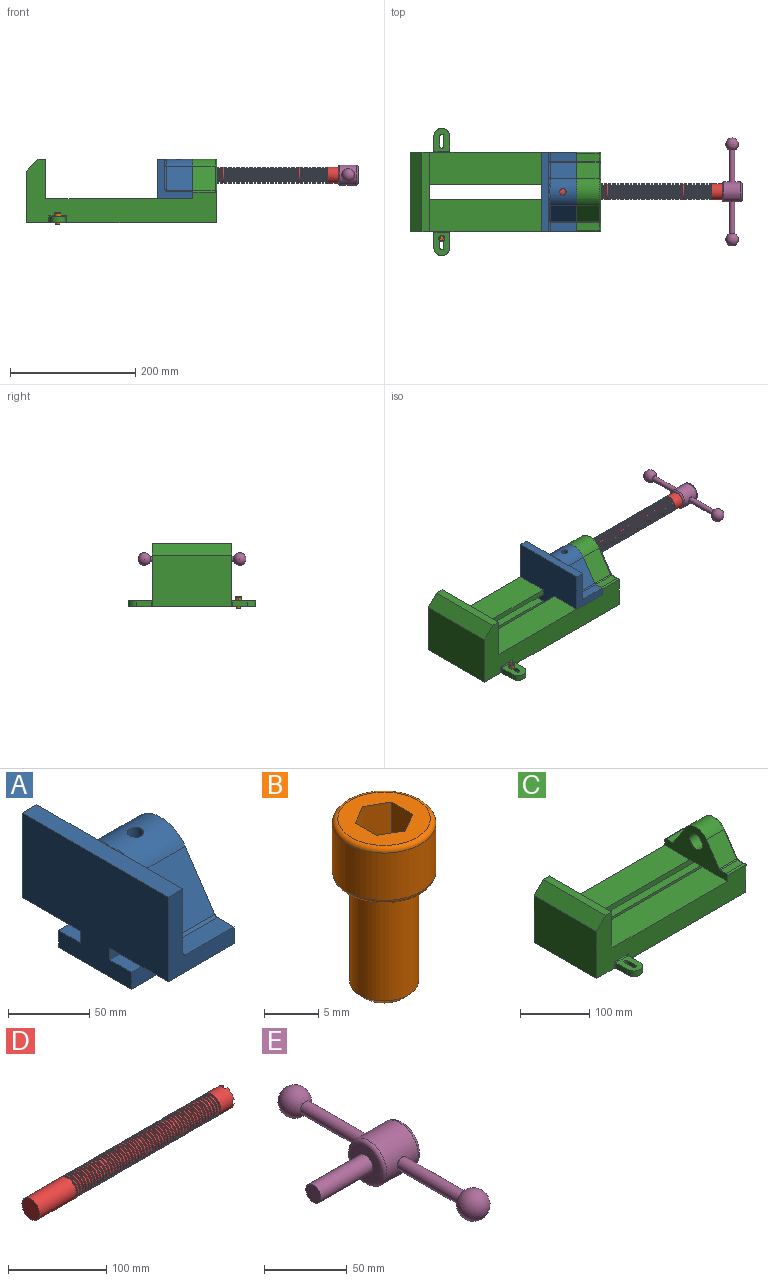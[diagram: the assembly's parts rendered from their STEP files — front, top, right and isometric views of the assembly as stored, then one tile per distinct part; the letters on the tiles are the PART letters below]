
ASSEMBLY  parts=5 mates=5
PART A: 36 faces, bbox 57.2x127x89 mm
  f0: plane 57.15x50.8mm, normal (0,0,-1), area 2903.2mm2, adj f6,f9,f10,f23
  f1: cylinder r=12.7mm len=44.45mm, axis (1,0,0), area 3464.3mm2, adj f6,f15,f16
  f2: plane 41.91x14.52mm, normal (0,0,1), area 608.5mm2, adj f6,f11,f24,f25
  f3: plane 51.86x48.26mm, normal (1,0,0), area 1495.7mm2, adj f8,f10,f31,f33,f35
  f4: plane 51.86x48.26mm, normal (1,0,0), area 1495.7mm2, adj f8,f11,f24,f28,f29
  f5: plane 57.15x50.8mm, normal (0,0,-1), area 2903.2mm2, adj f6,f9,f11,f22
  f6: plane 127x85.09mm, normal (1,0,0), area 5190.6mm2, adj f0,f1,f2,f5,f7,f10,f11,f12
  f7: plane 41.91x14.52mm, normal (0,0,1), area 608.5mm2, adj f6,f10,f30,f31
  f8: plane 127x12.7mm, normal (0,0,1), area 1612.9mm2, adj f3,f4,f9,f10,f11,f26,f34
  f9: plane 127x85.09mm, normal (-1,0,0), area 9096.8mm2, adj f0,f5,f8,f10,f11,f17,f18,f19
  f10: plane 63.5x57.15mm, normal (0,-1,0), area 1372.3mm2, adj f0,f3,f6,f7,f8,f9,f31
  f11: plane 63.5x57.15mm, normal (0,1,0), area 1372.3mm2, adj f2,f4,f5,f6,f8,f9,f24
  f12: plane 41.91x38.43mm, normal (0,-0.83,0.56), area 1939.2mm2, adj f6,f13,f30,f33
  f13: cylinder r=25.4mm len=44.45mm, axis (1,0,0), area 2026.5mm2, adj f6,f12,f14,f16,f26,f28,f34,f35
  f14: plane 41.91x38.43mm, normal (0,0.83,0.56), area 1939.2mm2, adj f6,f13,f25,f29
  f15: plane 25.4x25.4mm, normal (1,0,0), area 506.7mm2, adj f1
  f16: cylinder r=5.08mm len=13.76mm, axis (0,0,1), area 414mm2, adj f1,f13
  f17: plane 57.15x19.05mm, normal (0,0,1), area 1088.7mm2, adj f6,f9,f18,f23
  f18: plane 57.15x12.7mm, normal (0,-1,0), area 725.8mm2, adj f6,f9,f17,f19
  f19: plane 63.5x57.15mm, normal (0,0,-1), area 3629mm2, adj f6,f9,f18,f20
  f20: plane 57.15x12.7mm, normal (0,1,0), area 725.8mm2, adj f6,f9,f19,f21
  f21: plane 57.15x19.05mm, normal (0,0,1), area 1088.7mm2, adj f6,f9,f20,f22
  f22: plane 57.15x8.89mm, normal (0,1,0), area 508.1mm2, adj f5,f6,f9,f21
  f23: plane 57.15x8.89mm, normal (0,-1,0), area 508.1mm2, adj f0,f6,f9,f17
  f24: cylinder r=2.54mm len=14.52mm, axis (0,-1,0), area 57.9mm2, adj f2,f4,f11,f27
  f25: cylinder r=2.54mm len=41.91mm, axis (1,0,0), area 104.3mm2, adj f2,f6,f14,f27
  f26: bspline ~12.24x2.8mm, area 20.9mm2, adj f8,f13,f28
  f27: sphere r=2.54mm, area 6.3mm2, adj f24,f25,f29
  f28: torus R=27.94mm, axis (1,0,0), area 57.8mm2, adj f4,f13,f26,f29
  f29: cylinder r=2.54mm len=39.84mm, axis (0,-0.56,0.83), area 184.6mm2, adj f4,f14,f27,f28
  f30: cylinder r=2.54mm len=41.91mm, axis (1,0,0), area 104.3mm2, adj f6,f7,f12,f32
  f31: cylinder r=2.54mm len=14.52mm, axis (0,-1,0), area 57.9mm2, adj f3,f7,f10,f32
  f32: sphere r=2.54mm, area 6.3mm2, adj f30,f31,f33
  f33: cylinder r=2.54mm len=39.84mm, axis (0,-0.56,-0.83), area 184.6mm2, adj f3,f12,f32,f35
  f34: bspline ~12.24x2.8mm, area 20.9mm2, adj f8,f13,f35
  f35: torus R=27.94mm, axis (1,0,0), area 57.8mm2, adj f3,f13,f33,f34
PART B: 15 faces, bbox 10.3x10.3x19.1 mm
  f0: plane 8.51x8.51mm, normal (0,0,1), area 37.2mm2, adj f5,f6,f7,f8,f9,f10,f14
  f1: cylinder r=3.17mm len=11.94mm, axis (0,0,1), area 238.2mm2, adj f4,f12
  f2: plane 4.83x4.83mm, normal (0,0,-1), area 18.3mm2, adj f12
  f3: cylinder r=4.76mm len=9.53mm, axis (0,0,-1), area 159.6mm2, adj f13,f14
  f4: plane 8.51x8.51mm, normal (0,0,-1), area 25.2mm2, adj f1,f13
  f5: plane 4.83x2.38mm, normal (-0.5,-0.87,0), area 13.3mm2, adj f0,f6,f10,f11
  f6: plane 4.83x2.38mm, normal (0.5,-0.87,0), area 13.3mm2, adj f0,f5,f7,f11
  f7: plane 4.83x2.75mm, normal (1,0,0), area 13.3mm2, adj f0,f6,f8,f11
  f8: plane 4.83x2.38mm, normal (0.5,0.87,0), area 13.3mm2, adj f0,f7,f9,f11
  f9: plane 4.83x2.38mm, normal (-0.5,0.87,0), area 13.3mm2, adj f0,f8,f10,f11
  f10: plane 4.83x2.75mm, normal (-1,0,0), area 13.3mm2, adj f0,f5,f9,f11
  f11: plane 5.5x4.76mm, normal (0,0,1), area 19.6mm2, adj f5,f6,f7,f8,f9,f10
  f12: cone r=3.17mm half-angle=45deg, axis (0,0,1), area 18.9mm2, adj f1,f2
  f13: torus R=4.25mm, axis (0,0,1), area 23mm2, adj f3,f4
  f14: torus R=4.25mm, axis (0,0,1), area 23mm2, adj f0,f3
PART C: 61 faces, bbox 304.8x203.2x103.7 mm
  f0: plane 304.8x101.6mm, normal (0,1,0), area 13520.3mm2, adj f3,f4,f5,f6,f7,f8,f9,f16
  f1: plane 304.8x101.6mm, normal (0,-1,0), area 13520.3mm2, adj f2,f3,f5,f6,f7,f8,f9,f16
  f2: plane 234.95x50.8mm, normal (0,0,1), area 11935.5mm2, adj f1,f5,f16,f26
  f3: plane 127x99.06mm, normal (1,0,0), area 7097.5mm2, adj f0,f1,f9,f14,f17,f18,f19,f20
  f4: plane 234.95x50.8mm, normal (0,0,1), area 11935.5mm2, adj f0,f5,f16,f27
  f5: plane 127x101.6mm, normal (1,0,0), area 9516.1mm2, adj f0,f1,f2,f4,f6,f9,f18,f19
  f6: plane 127x12.7mm, normal (0,0,1), area 1612.9mm2, adj f0,f1,f5,f7
  f7: plane 127x19.05mm, normal (-0.71,0,0.71), area 3421.5mm2, adj f0,f1,f6,f8
  f8: plane 127x82.55mm, normal (-1,0,0), area 10483.8mm2, adj f0,f1,f7,f9
  f9: plane 304.8x203.2mm, normal (0,0,-1), area 33298.3mm2, adj f0,f1,f3,f5,f8,f21,f22,f39
  f10: plane 35.56x11.98mm, normal (0,0,1), area 426mm2, adj f16,f28,f29,f30
  f11: plane 38.43x35.56mm, normal (0,0.83,0.56), area 1645.4mm2, adj f12,f16,f29,f32
  f12: cylinder r=25.4mm len=42.19mm, axis (1,0,0), area 1770.2mm2, adj f11,f13,f16,f33
  f13: plane 38.43x35.56mm, normal (0,-0.83,0.56), area 1645.4mm2, adj f12,f16,f34,f35
  f14: cylinder r=12.7mm len=38.1mm, axis (1,0,0), area 3040.2mm2, adj f3,f16
  f15: plane 35.56x11.98mm, normal (0,0,1), area 426mm2, adj f16,f34,f36,f38
  f16: plane 127x63.5mm, normal (-1,0,0), area 4155.5mm2, adj f0,f1,f2,f4,f10,f11,f12,f13
  f17: plane 38.1x25.4mm, normal (0,0,-1), area 967.7mm2, adj f3,f16,f26,f27
  f18: plane 273.05x19.05mm, normal (0,0,-1), area 5201.6mm2, adj f3,f5,f19,f26
  f19: plane 273.05x12.7mm, normal (0,1,0), area 3467.7mm2, adj f3,f5,f18,f20
  f20: plane 273.05x19.05mm, normal (0,0,1), area 5201.6mm2, adj f3,f5,f19,f21
  f21: plane 273.05x16.51mm, normal (0,1,0), area 4508.1mm2, adj f3,f5,f9,f20
  f22: plane 273.05x16.51mm, normal (0,-1,0), area 4508.1mm2, adj f3,f5,f9,f23
  f23: plane 273.05x19.05mm, normal (0,0,1), area 5201.6mm2, adj f3,f5,f22,f24
  f24: plane 273.05x12.7mm, normal (0,-1,0), area 3467.7mm2, adj f3,f5,f23,f25
  f25: plane 273.05x19.05mm, normal (0,0,-1), area 5201.6mm2, adj f3,f5,f24,f27
  f26: plane 273.05x8.89mm, normal (0,1,0), area 2427.4mm2, adj f2,f3,f5,f17,f18
  f27: plane 273.05x8.89mm, normal (0,-1,0), area 2427.4mm2, adj f3,f4,f5,f17,f25
  f28: cylinder r=2.54mm len=38.1mm, axis (1,0,0), area 148.3mm2, adj f0,f10,f16,f30
  f29: cylinder r=2.54mm len=35.56mm, axis (-1,0,0), area 88.5mm2, adj f10,f11,f16,f31
  f30: cylinder r=2.54mm len=14.52mm, axis (0,1,0), area 54.3mm2, adj f3,f10,f28,f31
  f31: torus R=5.08mm, axis (-1,0,0), area 13.5mm2, adj f3,f29,f30,f32
  f32: cylinder r=2.54mm len=39.84mm, axis (0,0.56,-0.83), area 184.6mm2, adj f3,f11,f31,f33
  f33: torus R=22.86mm, axis (-1,0,0), area 191.4mm2, adj f3,f12,f32,f35
  f34: cylinder r=2.54mm len=35.56mm, axis (-1,0,0), area 88.5mm2, adj f13,f15,f16,f37
  f35: cylinder r=2.54mm len=39.84mm, axis (0,0.56,0.83), area 184.6mm2, adj f3,f13,f33,f37
  f36: cylinder r=2.54mm len=38.1mm, axis (-1,0,0), area 148.3mm2, adj f1,f15,f16,f38
  f37: torus R=5.08mm, axis (-1,0,0), area 13.5mm2, adj f3,f34,f35,f38
  f38: cylinder r=2.54mm len=14.52mm, axis (0,1,0), area 54.3mm2, adj f3,f15,f36,f37
  f39: plane 23.88x9.53mm, normal (-1,0,0), area 227.4mm2, adj f9,f45,f46,f60
  f40: plane 23.88x9.53mm, normal (1,0,0), area 227.4mm2, adj f9,f45,f46,f58
  f41: cylinder r=3.3mm len=9.53mm, axis (0,0,-1), area 98.8mm2, adj f9,f42,f44,f46
  f42: plane 15.62x9.53mm, normal (-1,0,0), area 148.8mm2, adj f9,f41,f43,f46
  f43: cylinder r=3.3mm len=9.53mm, axis (0,0,-1), area 98.8mm2, adj f9,f42,f44,f46
  f44: plane 15.62x9.53mm, normal (1,0,0), area 148.8mm2, adj f9,f41,f43,f46
  f45: cylinder r=12.7mm len=25.4mm, axis (0,0,-1), area 380mm2, adj f9,f39,f40,f46
  f46: plane 36.58x25.4mm, normal (0,0,1), area 722.4mm2, adj f39,f40,f41,f42,f43,f44,f45,f59
  f47: plane 23.88x9.53mm, normal (-1,0,0), area 227.4mm2, adj f9,f53,f54,f56
  f48: plane 23.88x9.53mm, normal (1,0,0), area 227.4mm2, adj f9,f53,f54,f55
  f49: cylinder r=3.3mm len=9.53mm, axis (0,0,-1), area 98.8mm2, adj f9,f50,f52,f54
  f50: plane 15.62x9.53mm, normal (-1,0,0), area 148.8mm2, adj f9,f49,f51,f54
  f51: cylinder r=3.3mm len=9.53mm, axis (0,0,-1), area 98.8mm2, adj f9,f50,f52,f54
  f52: plane 15.62x9.53mm, normal (1,0,0), area 148.8mm2, adj f9,f49,f51,f54
  f53: cylinder r=12.7mm len=25.4mm, axis (0,0,-1), area 380mm2, adj f9,f47,f48,f54
  f54: plane 36.58x25.4mm, normal (0,0,1), area 722.4mm2, adj f47,f48,f49,f50,f51,f52,f53,f57
  f55: cylinder r=1.52mm len=11.05mm, axis (0,0,-1), area 24.1mm2, adj f0,f9,f48,f57
  f56: cylinder r=1.52mm len=11.05mm, axis (0,0,1), area 24.1mm2, adj f0,f9,f47,f57
  f57: cylinder r=1.52mm len=28.45mm, axis (1,0,0), area 63.5mm2, adj f0,f54,f55,f56
  f58: cylinder r=1.52mm len=11.05mm, axis (0,0,1), area 24.1mm2, adj f1,f9,f40,f59
  f59: cylinder r=1.52mm len=28.45mm, axis (-1,0,0), area 63.5mm2, adj f1,f46,f58,f60
  f60: cylinder r=1.52mm len=11.05mm, axis (0,0,-1), area 24.1mm2, adj f1,f9,f39,f59
PART D: 220 faces, bbox 279.4x25.4x25.4 mm
  f0: cylinder r=12.7mm len=25.4mm, axis (-1,0,0), area 1468.2mm2, adj f1,f2,f3,f5,f7,f208,f209,f210
  f1: plane 9.9x9.9mm, normal (1,0,0), area 62.3mm2, adj f0,f4,f213,f216
  f2: plane 9.9x9.9mm, normal (1,0,0), area 62.3mm2, adj f0,f4,f210,f218
  f3: plane 9.9x9.9mm, normal (1,0,0), area 62.3mm2, adj f0,f4,f209,f212
  f4: cylinder r=6.35mm len=25.4mm, axis (1,0,0), area 960.3mm2, adj f1,f2,f3,f5,f6,f208,f209,f210
  f5: plane 9.9x9.9mm, normal (1,0,0), area 62.3mm2, adj f0,f4,f215,f217
  f6: plane 12.7x12.7mm, normal (1,0,0), area 126.7mm2, adj f4
  f7: cone r=12.7mm half-angle=76deg, axis (1,0,0), area 188mm2, adj f0,f9
  f8: cone r=10.16mm half-angle=76deg, axis (-1,0,0), area 188mm2, adj f9,f10
  f9: cylinder r=10.16mm len=20.32mm, axis (1,0,0), area 81.1mm2, adj f7,f8
  f10: cylinder r=12.7mm len=25.4mm, axis (-1,0,0), area 131.7mm2, adj f8,f11
  f11: cone r=12.7mm half-angle=76deg, axis (1,0,0), area 188mm2, adj f10,f13
  f12: cone r=10.16mm half-angle=76deg, axis (-1,0,0), area 188mm2, adj f13,f14
  f13: cylinder r=10.16mm len=20.32mm, axis (1,0,0), area 81.1mm2, adj f11,f12
  f14: cylinder r=12.7mm len=25.4mm, axis (-1,0,0), area 131.7mm2, adj f12,f15
  f15: cone r=12.7mm half-angle=76deg, axis (1,0,0), area 188mm2, adj f14,f17
  f16: cone r=10.16mm half-angle=76deg, axis (-1,0,0), area 188mm2, adj f17,f18
  f17: cylinder r=10.16mm len=20.32mm, axis (1,0,0), area 81.1mm2, adj f15,f16
  f18: cylinder r=12.7mm len=25.4mm, axis (-1,0,0), area 131.7mm2, adj f16,f19
  f19: cone r=12.7mm half-angle=76deg, axis (1,0,0), area 188mm2, adj f18,f21
  f20: cone r=10.16mm half-angle=76deg, axis (-1,0,0), area 188mm2, adj f21,f22
  f21: cylinder r=10.16mm len=20.32mm, axis (1,0,0), area 81.1mm2, adj f19,f20
  f22: cylinder r=12.7mm len=25.4mm, axis (-1,0,0), area 131.7mm2, adj f20,f23
  f23: cone r=12.7mm half-angle=76deg, axis (1,0,0), area 188mm2, adj f22,f25
  f24: cone r=10.16mm half-angle=76deg, axis (-1,0,0), area 188mm2, adj f25,f26
  f25: cylinder r=10.16mm len=20.32mm, axis (1,0,0), area 81.1mm2, adj f23,f24
  f26: cylinder r=12.7mm len=25.4mm, axis (-1,0,0), area 131.7mm2, adj f24,f27
  f27: cone r=12.7mm half-angle=76deg, axis (1,0,0), area 188mm2, adj f26,f29
  f28: cone r=10.16mm half-angle=76deg, axis (-1,0,0), area 188mm2, adj f29,f30
  f29: cylinder r=10.16mm len=20.32mm, axis (1,0,0), area 81.1mm2, adj f27,f28
  f30: cylinder r=12.7mm len=25.4mm, axis (-1,0,0), area 131.7mm2, adj f28,f31
  f31: cone r=12.7mm half-angle=76deg, axis (1,0,0), area 188mm2, adj f30,f33
  f32: cone r=10.16mm half-angle=76deg, axis (-1,0,0), area 188mm2, adj f33,f34
  f33: cylinder r=10.16mm len=20.32mm, axis (1,0,0), area 81.1mm2, adj f31,f32
  f34: cylinder r=12.7mm len=25.4mm, axis (-1,0,0), area 131.7mm2, adj f32,f35
  f35: cone r=12.7mm half-angle=76deg, axis (1,0,0), area 188mm2, adj f34,f37
  f36: cone r=10.16mm half-angle=76deg, axis (-1,0,0), area 188mm2, adj f37,f38
  f37: cylinder r=10.16mm len=20.32mm, axis (1,0,0), area 81.1mm2, adj f35,f36
  f38: cylinder r=12.7mm len=25.4mm, axis (-1,0,0), area 131.7mm2, adj f36,f39
  f39: cone r=12.7mm half-angle=76deg, axis (1,0,0), area 188mm2, adj f38,f41
  f40: cone r=10.16mm half-angle=76deg, axis (-1,0,0), area 188mm2, adj f41,f42
  f41: cylinder r=10.16mm len=20.32mm, axis (1,0,0), area 81.1mm2, adj f39,f40
  f42: cylinder r=12.7mm len=25.4mm, axis (-1,0,0), area 131.7mm2, adj f40,f43
  f43: cone r=12.7mm half-angle=76deg, axis (1,0,0), area 188mm2, adj f42,f45
  f44: cone r=10.16mm half-angle=76deg, axis (-1,0,0), area 188mm2, adj f45,f46
  f45: cylinder r=10.16mm len=20.32mm, axis (1,0,0), area 81.1mm2, adj f43,f44
  f46: cylinder r=12.7mm len=25.4mm, axis (-1,0,0), area 131.7mm2, adj f44,f47
  f47: cone r=12.7mm half-angle=76deg, axis (1,0,0), area 188mm2, adj f46,f49
  f48: cone r=10.16mm half-angle=76deg, axis (-1,0,0), area 188mm2, adj f49,f50
  f49: cylinder r=10.16mm len=20.32mm, axis (1,0,0), area 81.1mm2, adj f47,f48
  f50: cylinder r=12.7mm len=25.4mm, axis (-1,0,0), area 131.7mm2, adj f48,f51
  f51: cone r=12.7mm half-angle=76deg, axis (1,0,0), area 188mm2, adj f50,f53
  f52: cone r=10.16mm half-angle=76deg, axis (-1,0,0), area 188mm2, adj f53,f54
  f53: cylinder r=10.16mm len=20.32mm, axis (1,0,0), area 81.1mm2, adj f51,f52
  f54: cylinder r=12.7mm len=25.4mm, axis (-1,0,0), area 131.7mm2, adj f52,f55
  f55: cone r=12.7mm half-angle=76deg, axis (1,0,0), area 188mm2, adj f54,f57
  f56: cone r=10.16mm half-angle=76deg, axis (-1,0,0), area 188mm2, adj f57,f58
  f57: cylinder r=10.16mm len=20.32mm, axis (1,0,0), area 81.1mm2, adj f55,f56
  f58: cylinder r=12.7mm len=25.4mm, axis (-1,0,0), area 131.7mm2, adj f56,f59
  f59: cone r=12.7mm half-angle=76deg, axis (1,0,0), area 188mm2, adj f58,f61
  f60: cone r=10.16mm half-angle=76deg, axis (-1,0,0), area 188mm2, adj f61,f62
  f61: cylinder r=10.16mm len=20.32mm, axis (1,0,0), area 81.1mm2, adj f59,f60
  f62: cylinder r=12.7mm len=25.4mm, axis (-1,0,0), area 131.7mm2, adj f60,f63
  f63: cone r=12.7mm half-angle=76deg, axis (1,0,0), area 188mm2, adj f62,f65
  f64: cone r=10.16mm half-angle=76deg, axis (-1,0,0), area 188mm2, adj f65,f66
  f65: cylinder r=10.16mm len=20.32mm, axis (1,0,0), area 81.1mm2, adj f63,f64
  f66: cylinder r=12.7mm len=25.4mm, axis (-1,0,0), area 131.7mm2, adj f64,f67
  f67: cone r=12.7mm half-angle=76deg, axis (1,0,0), area 188mm2, adj f66,f69
  f68: cone r=10.16mm half-angle=76deg, axis (-1,0,0), area 188mm2, adj f69,f70
  f69: cylinder r=10.16mm len=20.32mm, axis (1,0,0), area 81.1mm2, adj f67,f68
  f70: cylinder r=12.7mm len=25.4mm, axis (-1,0,0), area 131.7mm2, adj f68,f71
  f71: cone r=12.7mm half-angle=76deg, axis (1,0,0), area 188mm2, adj f70,f73
  f72: cone r=10.16mm half-angle=76deg, axis (-1,0,0), area 188mm2, adj f73,f74
  f73: cylinder r=10.16mm len=20.32mm, axis (1,0,0), area 81.1mm2, adj f71,f72
  f74: cylinder r=12.7mm len=25.4mm, axis (-1,0,0), area 131.7mm2, adj f72,f75
  f75: cone r=12.7mm half-angle=76deg, axis (1,0,0), area 188mm2, adj f74,f77
  f76: cone r=10.16mm half-angle=76deg, axis (-1,0,0), area 188mm2, adj f77,f78
  f77: cylinder r=10.16mm len=20.32mm, axis (1,0,0), area 81.1mm2, adj f75,f76
  f78: cylinder r=12.7mm len=25.4mm, axis (-1,0,0), area 131.7mm2, adj f76,f79
  f79: cone r=12.7mm half-angle=76deg, axis (1,0,0), area 188mm2, adj f78,f81
  f80: cone r=10.16mm half-angle=76deg, axis (-1,0,0), area 188mm2, adj f81,f82
  f81: cylinder r=10.16mm len=20.32mm, axis (1,0,0), area 81.1mm2, adj f79,f80
  f82: cylinder r=12.7mm len=25.4mm, axis (-1,0,0), area 131.7mm2, adj f80,f83
  f83: cone r=12.7mm half-angle=76deg, axis (1,0,0), area 188mm2, adj f82,f85
  f84: cone r=10.16mm half-angle=76deg, axis (-1,0,0), area 188mm2, adj f85,f86
  f85: cylinder r=10.16mm len=20.32mm, axis (1,0,0), area 81.1mm2, adj f83,f84
  f86: cylinder r=12.7mm len=25.4mm, axis (-1,0,0), area 131.7mm2, adj f84,f87
  f87: cone r=12.7mm half-angle=76deg, axis (1,0,0), area 188mm2, adj f86,f89
  f88: cone r=10.16mm half-angle=76deg, axis (-1,0,0), area 188mm2, adj f89,f90
  f89: cylinder r=10.16mm len=20.32mm, axis (1,0,0), area 81.1mm2, adj f87,f88
  f90: cylinder r=12.7mm len=25.4mm, axis (-1,0,0), area 131.7mm2, adj f88,f91
  f91: cone r=12.7mm half-angle=76deg, axis (1,0,0), area 188mm2, adj f90,f93
  f92: cone r=10.16mm half-angle=76deg, axis (-1,0,0), area 188mm2, adj f93,f94
  f93: cylinder r=10.16mm len=20.32mm, axis (1,0,0), area 81.1mm2, adj f91,f92
  f94: cylinder r=12.7mm len=25.4mm, axis (-1,0,0), area 131.7mm2, adj f92,f95
  f95: cone r=12.7mm half-angle=76deg, axis (1,0,0), area 188mm2, adj f94,f97
  f96: cone r=10.16mm half-angle=76deg, axis (-1,0,0), area 188mm2, adj f97,f98
  f97: cylinder r=10.16mm len=20.32mm, axis (1,0,0), area 81.1mm2, adj f95,f96
  f98: cylinder r=12.7mm len=25.4mm, axis (-1,0,0), area 131.7mm2, adj f96,f99
  f99: cone r=12.7mm half-angle=76deg, axis (1,0,0), area 188mm2, adj f98,f101
  f100: cone r=10.16mm half-angle=76deg, axis (-1,0,0), area 188mm2, adj f101,f102
  f101: cylinder r=10.16mm len=20.32mm, axis (1,0,0), area 81.1mm2, adj f99,f100
  f102: cylinder r=12.7mm len=25.4mm, axis (-1,0,0), area 131.7mm2, adj f100,f103
  f103: cone r=12.7mm half-angle=76deg, axis (1,0,0), area 188mm2, adj f102,f105
  f104: cone r=10.16mm half-angle=76deg, axis (-1,0,0), area 188mm2, adj f105,f106
  f105: cylinder r=10.16mm len=20.32mm, axis (1,0,0), area 81.1mm2, adj f103,f104
  f106: cylinder r=12.7mm len=25.4mm, axis (-1,0,0), area 131.7mm2, adj f104,f107
  f107: cone r=12.7mm half-angle=76deg, axis (1,0,0), area 188mm2, adj f106,f109
  f108: cone r=10.16mm half-angle=76deg, axis (-1,0,0), area 188mm2, adj f109,f110
  f109: cylinder r=10.16mm len=20.32mm, axis (1,0,0), area 81.1mm2, adj f107,f108
  f110: cylinder r=12.7mm len=25.4mm, axis (-1,0,0), area 131.7mm2, adj f108,f111
  f111: cone r=12.7mm half-angle=76deg, axis (1,0,0), area 188mm2, adj f110,f113
  f112: cone r=10.16mm half-angle=76deg, axis (-1,0,0), area 188mm2, adj f113,f114
  f113: cylinder r=10.16mm len=20.32mm, axis (1,0,0), area 81.1mm2, adj f111,f112
  f114: cylinder r=12.7mm len=25.4mm, axis (-1,0,0), area 131.7mm2, adj f112,f115
  f115: cone r=12.7mm half-angle=76deg, axis (1,0,0), area 188mm2, adj f114,f117
  f116: cone r=10.16mm half-angle=76deg, axis (-1,0,0), area 188mm2, adj f117,f118
  f117: cylinder r=10.16mm len=20.32mm, axis (1,0,0), area 81.1mm2, adj f115,f116
  f118: cylinder r=12.7mm len=25.4mm, axis (-1,0,0), area 131.7mm2, adj f116,f119
  f119: cone r=12.7mm half-angle=76deg, axis (1,0,0), area 188mm2, adj f118,f121
  f120: cone r=10.16mm half-angle=76deg, axis (-1,0,0), area 188mm2, adj f121,f122
  f121: cylinder r=10.16mm len=20.32mm, axis (1,0,0), area 81.1mm2, adj f119,f120
  f122: cylinder r=12.7mm len=25.4mm, axis (-1,0,0), area 131.7mm2, adj f120,f123
  f123: cone r=12.7mm half-angle=76deg, axis (1,0,0), area 188mm2, adj f122,f125
  f124: cone r=10.16mm half-angle=76deg, axis (-1,0,0), area 188mm2, adj f125,f126
  f125: cylinder r=10.16mm len=20.32mm, axis (1,0,0), area 81.1mm2, adj f123,f124
  f126: cylinder r=12.7mm len=25.4mm, axis (-1,0,0), area 131.7mm2, adj f124,f127
  f127: cone r=12.7mm half-angle=76deg, axis (1,0,0), area 188mm2, adj f126,f129
  f128: cone r=10.16mm half-angle=76deg, axis (-1,0,0), area 188mm2, adj f129,f130
  f129: cylinder r=10.16mm len=20.32mm, axis (1,0,0), area 81.1mm2, adj f127,f128
  f130: cylinder r=12.7mm len=25.4mm, axis (-1,0,0), area 131.7mm2, adj f128,f131
  f131: cone r=12.7mm half-angle=76deg, axis (1,0,0), area 188mm2, adj f130,f133
  f132: cone r=10.16mm half-angle=76deg, axis (-1,0,0), area 188mm2, adj f133,f134
  f133: cylinder r=10.16mm len=20.32mm, axis (1,0,0), area 81.1mm2, adj f131,f132
  f134: cylinder r=12.7mm len=25.4mm, axis (-1,0,0), area 131.7mm2, adj f132,f135
  f135: cone r=12.7mm half-angle=76deg, axis (1,0,0), area 188mm2, adj f134,f137
  f136: cone r=10.16mm half-angle=76deg, axis (-1,0,0), area 188mm2, adj f137,f138
  f137: cylinder r=10.16mm len=20.32mm, axis (1,0,0), area 81.1mm2, adj f135,f136
  f138: cylinder r=12.7mm len=25.4mm, axis (-1,0,0), area 131.7mm2, adj f136,f139
  f139: cone r=12.7mm half-angle=76deg, axis (1,0,0), area 188mm2, adj f138,f141
  f140: cone r=10.16mm half-angle=76deg, axis (-1,0,0), area 188mm2, adj f141,f142
  f141: cylinder r=10.16mm len=20.32mm, axis (1,0,0), area 81.1mm2, adj f139,f140
  f142: cylinder r=12.7mm len=25.4mm, axis (-1,0,0), area 131.7mm2, adj f140,f143
  f143: cone r=12.7mm half-angle=76deg, axis (1,0,0), area 188mm2, adj f142,f145
  f144: cone r=10.16mm half-angle=76deg, axis (-1,0,0), area 188mm2, adj f145,f146
  f145: cylinder r=10.16mm len=20.32mm, axis (1,0,0), area 81.1mm2, adj f143,f144
  f146: cylinder r=12.7mm len=25.4mm, axis (-1,0,0), area 131.7mm2, adj f144,f147
  f147: cone r=12.7mm half-angle=76deg, axis (1,0,0), area 188mm2, adj f146,f149
  f148: cone r=10.16mm half-angle=76deg, axis (-1,0,0), area 188mm2, adj f149,f150
  f149: cylinder r=10.16mm len=20.32mm, axis (1,0,0), area 81.1mm2, adj f147,f148
  f150: cylinder r=12.7mm len=25.4mm, axis (-1,0,0), area 131.7mm2, adj f148,f151
  f151: cone r=12.7mm half-angle=76deg, axis (1,0,0), area 188mm2, adj f150,f153
  f152: cone r=10.16mm half-angle=76deg, axis (-1,0,0), area 188mm2, adj f153,f154
  f153: cylinder r=10.16mm len=20.32mm, axis (1,0,0), area 81.1mm2, adj f151,f152
  f154: cylinder r=12.7mm len=25.4mm, axis (-1,0,0), area 131.7mm2, adj f152,f155
  f155: cone r=12.7mm half-angle=76deg, axis (1,0,0), area 188mm2, adj f154,f157
  f156: cone r=10.16mm half-angle=76deg, axis (-1,0,0), area 188mm2, adj f157,f158
  f157: cylinder r=10.16mm len=20.32mm, axis (1,0,0), area 81.1mm2, adj f155,f156
  f158: cylinder r=12.7mm len=25.4mm, axis (-1,0,0), area 131.7mm2, adj f156,f159
  f159: cone r=12.7mm half-angle=76deg, axis (1,0,0), area 188mm2, adj f158,f161
  f160: cone r=10.16mm half-angle=76deg, axis (-1,0,0), area 188mm2, adj f161,f162
  f161: cylinder r=10.16mm len=20.32mm, axis (1,0,0), area 81.1mm2, adj f159,f160
  f162: cylinder r=12.7mm len=25.4mm, axis (-1,0,0), area 131.7mm2, adj f160,f163
  f163: cone r=12.7mm half-angle=76deg, axis (1,0,0), area 188mm2, adj f162,f165
  f164: cone r=10.16mm half-angle=76deg, axis (-1,0,0), area 188mm2, adj f165,f166
  f165: cylinder r=10.16mm len=20.32mm, axis (1,0,0), area 81.1mm2, adj f163,f164
  f166: cylinder r=12.7mm len=25.4mm, axis (-1,0,0), area 131.7mm2, adj f164,f167
  f167: cone r=12.7mm half-angle=76deg, axis (1,0,0), area 188mm2, adj f166,f169
  f168: cone r=10.16mm half-angle=76deg, axis (-1,0,0), area 188mm2, adj f169,f170
  f169: cylinder r=10.16mm len=20.32mm, axis (1,0,0), area 81.1mm2, adj f167,f168
  f170: cylinder r=12.7mm len=25.4mm, axis (-1,0,0), area 131.7mm2, adj f168,f171
  f171: cone r=12.7mm half-angle=76deg, axis (1,0,0), area 188mm2, adj f170,f173
  f172: cone r=10.16mm half-angle=76deg, axis (-1,0,0), area 188mm2, adj f173,f174
  f173: cylinder r=10.16mm len=20.32mm, axis (1,0,0), area 81.1mm2, adj f171,f172
  f174: cylinder r=12.7mm len=25.4mm, axis (-1,0,0), area 131.7mm2, adj f172,f175
  f175: cone r=12.7mm half-angle=76deg, axis (1,0,0), area 188mm2, adj f174,f177
  f176: cone r=10.16mm half-angle=76deg, axis (-1,0,0), area 188mm2, adj f177,f178
  f177: cylinder r=10.16mm len=20.32mm, axis (1,0,0), area 81.1mm2, adj f175,f176
  f178: cylinder r=12.7mm len=25.4mm, axis (-1,0,0), area 131.7mm2, adj f176,f179
  f179: cone r=12.7mm half-angle=76deg, axis (1,0,0), area 188mm2, adj f178,f181
  f180: cone r=10.16mm half-angle=76deg, axis (-1,0,0), area 188mm2, adj f181,f182
  f181: cylinder r=10.16mm len=20.32mm, axis (1,0,0), area 81.1mm2, adj f179,f180
  f182: cylinder r=12.7mm len=25.4mm, axis (-1,0,0), area 131.7mm2, adj f180,f183
  f183: cone r=12.7mm half-angle=76deg, axis (1,0,0), area 188mm2, adj f182,f185
  f184: cone r=10.16mm half-angle=76deg, axis (-1,0,0), area 188mm2, adj f185,f186
  f185: cylinder r=10.16mm len=20.32mm, axis (1,0,0), area 81.1mm2, adj f183,f184
  f186: cylinder r=12.7mm len=25.4mm, axis (-1,0,0), area 131.7mm2, adj f184,f187
  f187: cone r=12.7mm half-angle=76deg, axis (1,0,0), area 188mm2, adj f186,f189
  f188: cone r=10.16mm half-angle=76deg, axis (-1,0,0), area 188mm2, adj f189,f190
  f189: cylinder r=10.16mm len=20.32mm, axis (1,0,0), area 81.1mm2, adj f187,f188
  f190: cylinder r=12.7mm len=25.4mm, axis (-1,0,0), area 131.7mm2, adj f188,f191
  f191: cone r=12.7mm half-angle=76deg, axis (1,0,0), area 188mm2, adj f190,f193
  f192: cone r=10.16mm half-angle=76deg, axis (-1,0,0), area 188mm2, adj f193,f194
  f193: cylinder r=10.16mm len=20.32mm, axis (1,0,0), area 81.1mm2, adj f191,f192
  f194: cylinder r=12.7mm len=25.4mm, axis (-1,0,0), area 131.7mm2, adj f192,f195
  f195: cone r=12.7mm half-angle=76deg, axis (1,0,0), area 188mm2, adj f194,f197
  f196: cone r=10.16mm half-angle=76deg, axis (-1,0,0), area 188mm2, adj f197,f198
  f197: cylinder r=10.16mm len=20.32mm, axis (1,0,0), area 81.1mm2, adj f195,f196
  f198: cylinder r=12.7mm len=25.4mm, axis (-1,0,0), area 131.7mm2, adj f196,f199
  f199: cone r=12.7mm half-angle=76deg, axis (1,0,0), area 188mm2, adj f198,f201
  f200: cone r=10.16mm half-angle=76deg, axis (-1,0,0), area 188mm2, adj f201,f202
  f201: cylinder r=10.16mm len=20.32mm, axis (1,0,0), area 81.1mm2, adj f199,f200
  f202: cylinder r=12.7mm len=25.4mm, axis (-1,0,0), area 131.7mm2, adj f200,f203
  f203: cone r=12.7mm half-angle=76deg, axis (1,0,0), area 188mm2, adj f202,f205
  f204: cone r=10.16mm half-angle=76deg, axis (-1,0,0), area 188mm2, adj f205,f207
  f205: cylinder r=10.16mm len=20.32mm, axis (1,0,0), area 81.1mm2, adj f203,f204
  f206: plane 25.4x25.4mm, normal (-1,0,0), area 506.7mm2, adj f207
  f207: cylinder r=12.7mm len=52.45mm, axis (-1,0,0), area 4185.4mm2, adj f204,f206
  f208: plane 6.88x5.08mm, normal (1,0,0), area 32.7mm2, adj f0,f4,f209,f210
  f209: plane 6.62x2.54mm, normal (0,-1,0), area 16.8mm2, adj f0,f3,f4,f208
  f210: plane 6.62x2.54mm, normal (0,1,0), area 16.8mm2, adj f0,f2,f4,f208
  f211: plane 6.88x5.08mm, normal (1,0,0), area 32.7mm2, adj f0,f4,f212,f213
  f212: plane 6.62x2.54mm, normal (0,0,1), area 16.8mm2, adj f0,f3,f4,f211
  f213: plane 6.62x2.54mm, normal (0,0,-1), area 16.8mm2, adj f0,f1,f4,f211
  f214: plane 6.88x5.08mm, normal (1,0,0), area 32.7mm2, adj f0,f4,f215,f216
  f215: plane 6.62x2.54mm, normal (0,1,0), area 16.8mm2, adj f0,f4,f5,f214
  f216: plane 6.62x2.54mm, normal (0,-1,0), area 16.8mm2, adj f0,f1,f4,f214
  f217: plane 6.62x2.54mm, normal (0,0,-1), area 16.8mm2, adj f0,f4,f5,f219
  f218: plane 6.62x2.54mm, normal (0,0,1), area 16.8mm2, adj f0,f2,f4,f219
  f219: plane 6.88x5.08mm, normal (1,0,0), area 32.7mm2, adj f0,f4,f217,f218
PART E: 11 faces, bbox 76.2x172.7x34.4 mm
  f0: sphere r=10.16mm, area 1231.8mm2, adj f1
  f1: cylinder r=4.45mm len=51.82mm, axis (0,1,0), area 1438.5mm2, adj f0,f4
  f2: sphere r=10.16mm, area 1231.8mm2, adj f3
  f3: cylinder r=4.45mm len=51.82mm, axis (0,1,0), area 1438.5mm2, adj f2,f4
  f4: cylinder r=15.88mm len=31.75mm, axis (-1,0,0), area 2534.7mm2, adj f1,f3,f9,f10
  f5: cylinder r=6.35mm len=44.45mm, axis (-1,0,0), area 1773.5mm2, adj f6,f8
  f6: plane 12.7x12.7mm, normal (-1,0,0), area 126.7mm2, adj f5
  f7: plane 26.67x26.67mm, normal (1,0,0), area 558.6mm2, adj f10
  f8: plane 26.67x26.67mm, normal (-1,0,0), area 432mm2, adj f5,f9
  f9: torus R=13.33mm, axis (1,0,0), area 374.8mm2, adj f4,f8
  f10: torus R=13.33mm, axis (1,0,0), area 374.8mm2, adj f4,f7
PLACE A t=(177.8,0,0)mm
PLACE B rot(axis=(0,0,-1),22.3deg) t=(-254,-74.42,9.52)mm
PLACE C at identity fixed
PLACE D rot(axis=(1,0,0),180deg) t=(177.8,0,152.4)mm
PLACE E rot(axis=(1,0,0),180deg) t=(156.21,0,152.4)mm
MATE fastened D.f4 <-> E.f5  axis (1,0,0) through (194.31,0,76.2)mm
MATE planar A.f0 <-> C.f2  axis (0,0,-1) through (-66.68,-38.1,38.1)mm
MATE pin_slot B.f1 <-> C.f41  axis (0,0,1) through (-254,-74.42,9.52)mm
MATE revolute D.f7 <-> A.f28  axis (-1,0,0) through (-82.55,0,76.2)mm
MATE cylindrical C.f12 <-> D.f7  axis (-1,0,0) through (-38.1,0,76.2)mm
